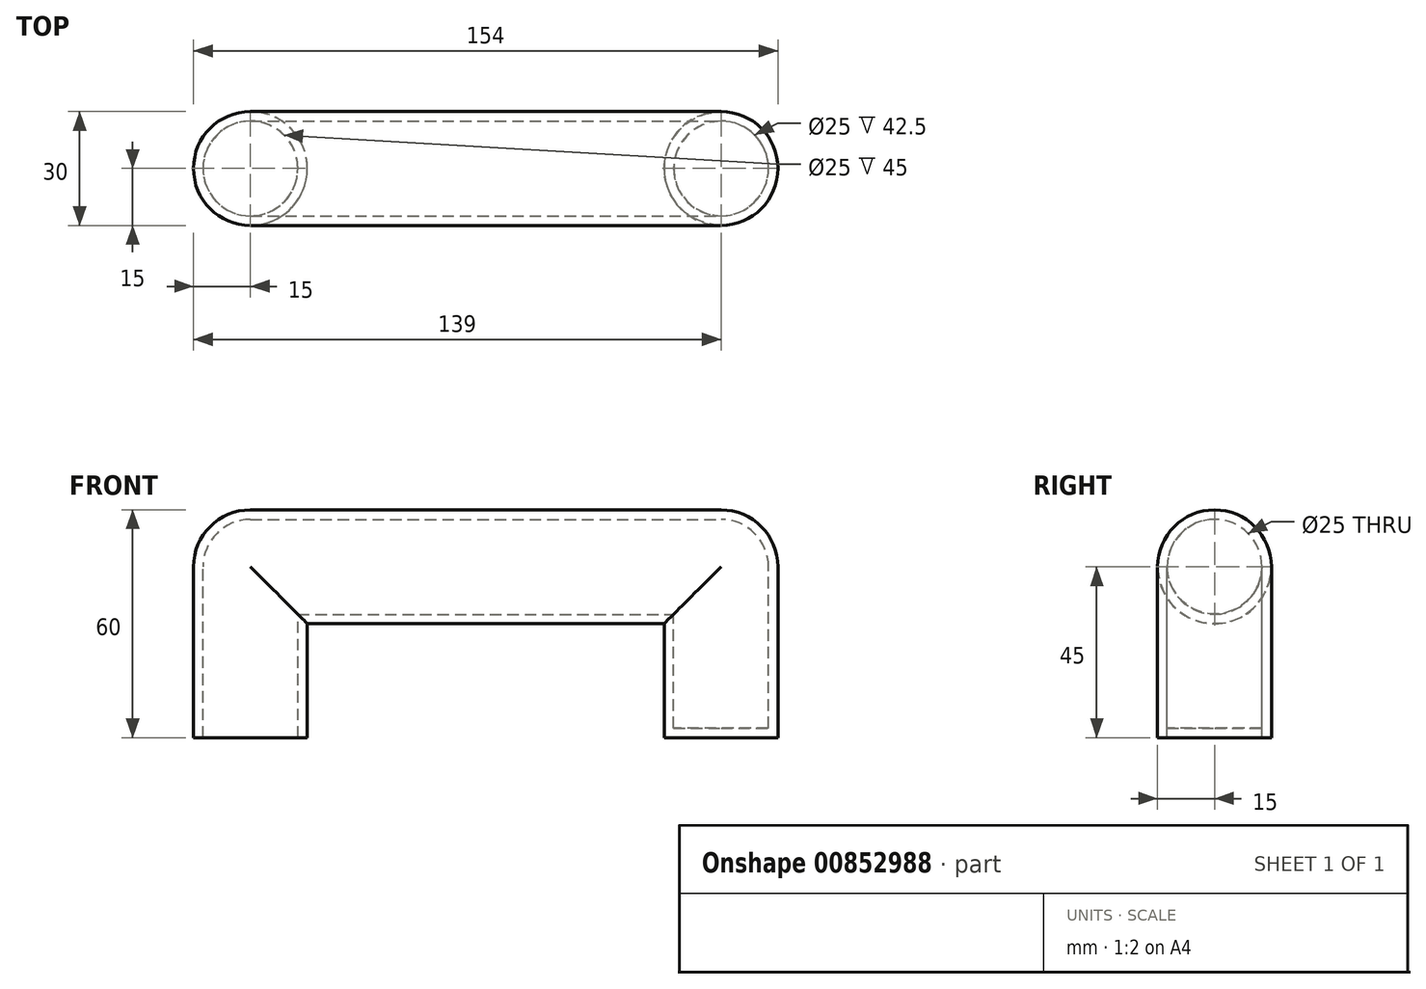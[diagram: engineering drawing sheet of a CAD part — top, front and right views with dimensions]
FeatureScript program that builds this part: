
annotation { "Feature Type Name" : "Feature", "Feature Type Description" : "" }
export const myFeature = defineFeature(function(context is Context, id is Id, definition is map)
    precondition{}
    {
        {
            var Q0;
            Q0=qCreatedBy(makeId("Front.planeOp"),FACE);
            var sketch = newSketch(context, id + "F0", { "sketchPlane" : qUnion([Q0])});
            skLineSegment(sketch, "E0.bottom", {"start": v(0, 0) * mm, "end": v(30, 0) * mm});
            skLineSegment(sketch, "E0.top", {"start": v(0, 60) * mm, "end": v(154, 60) * mm});
            skLineSegment(sketch, "E0.left", {"start": v(0, 0) * mm, "end": v(0, 60) * mm});
            skLineSegment(sketch, "E0.right", {"start": v(154, 0) * mm, "end": v(154, 60) * mm});
            skLineSegment(sketch, "E1.left", {"start": v(0, -22.26) * mm, "end": v(0, 0) * mm});
            skLineSegment(sketch, "E1.right", {"start": v(30, 0) * mm, "end": v(30, 30) * mm});
            skLineSegment(sketch, "E2.bottom", {"start": v(154, 0) * mm, "end": v(124, 0) * mm});
            skLineSegment(sketch, "E2.left", {"start": v(154, -22.26) * mm, "end": v(154, 0) * mm});
            skLineSegment(sketch, "E2.right", {"start": v(124, 0) * mm, "end": v(124, 30) * mm});
            skLineSegment(sketch, "E3", {"start": v(30, 30) * mm, "end": v(124, 30) * mm});
            skLineSegment(sketch, "E4.trimOffspring", {"start": v(124, 0) * mm, "end": v(154, 0) * mm});
            skSolve(sketch);
        }
        {
            var Q0;
            Q0=makeQuery(id+"F0.imprint","IMPRINT",FACE,{"disambiguationData":[TD([[makeQuery(id+"F0.imprint","IMPRINT",EDGE,{"derivedFrom":sQuery(id+"F0.wireOp",EDGE,"E0.top")}),-1.0]])]});
            extrude(context, id + "F1", {"entities" : qUnion([Q0]), "depth" : 30 * mm, "offsetDistance" : 25 * mm});
        }
        {
            var Q0;
            Q0=makeQuery(id+"F1.opExtrude","SWEPT_FACE",FACE,{"disambiguationData":[OSD([sQuery(id+"F0.wireOp",EDGE,"E0.top")])]});
            var Q1;
            Q1=makeQuery(id+"F1.opExtrude","CAP_EDGE",EDGE,{"disambiguationData":[OSD([sQuery(id+"F0.wireOp",EDGE,"E0.right"),sQuery(id+"F0.wireOp",EDGE,"E2.left")])],"isStart":false});
            var Q2;
            Q2=makeQuery(id+"F1.opExtrude","CAP_EDGE",EDGE,{"disambiguationData":[OSD([sQuery(id+"F0.wireOp",EDGE,"E2.right")])],"isStart":false});
            var Q3;
            Q3=makeQuery(id+"F1.opExtrude","CAP_EDGE",EDGE,{"disambiguationData":[OSD([sQuery(id+"F0.wireOp",EDGE,"E3")])],"isStart":false});
            var Q4;
            Q4=makeQuery(id+"F1.opExtrude","CAP_EDGE",EDGE,{"disambiguationData":[OSD([sQuery(id+"F0.wireOp",EDGE,"E1.right")])],"isStart":false});
            var Q5;
            Q5=makeQuery(id+"F1.opExtrude","CAP_EDGE",EDGE,{"disambiguationData":[OSD([sQuery(id+"F0.wireOp",EDGE,"E0.right"),sQuery(id+"F0.wireOp",EDGE,"E2.left")])],"isStart":true});
            var Q6;
            Q6=makeQuery(id+"F1.opExtrude","CAP_EDGE",EDGE,{"disambiguationData":[OSD([sQuery(id+"F0.wireOp",EDGE,"E2.right")])],"isStart":true});
            var Q7;
            Q7=makeQuery(id+"F1.opExtrude","CAP_EDGE",EDGE,{"disambiguationData":[OSD([sQuery(id+"F0.wireOp",EDGE,"E1.right")])],"isStart":true});
            var Q8;
            Q8=makeQuery(id+"F1.opExtrude","CAP_EDGE",EDGE,{"disambiguationData":[OSD([sQuery(id+"F0.wireOp",EDGE,"E3")])],"isStart":true});
            var Q9;
            Q9=makeQuery(id+"F1.opExtrude","CAP_EDGE",EDGE,{"disambiguationData":[OSD([sQuery(id+"F0.wireOp",EDGE,"E0.left"),sQuery(id+"F0.wireOp",EDGE,"E1.left")])],"isStart":true});
            var Q10;
            Q10=makeQuery(id+"F1.opExtrude","CAP_EDGE",EDGE,{"disambiguationData":[OSD([sQuery(id+"F0.wireOp",EDGE,"E0.left"),sQuery(id+"F0.wireOp",EDGE,"E1.left")])],"isStart":false});
            fillet(context, id + "F2", {"entities" : qUnion([Q0, Q1, Q2, Q3, Q4, Q5, Q6, Q7, Q8, Q9, Q10]), "radius" : 15 * mm, "allowEdgeOverflow" : false});
        }
        {
            var Q0;
            Q0=makeQuery(id+"F1.opExtrude","SWEPT_FACE",FACE,{"disambiguationData":[OSD([sQuery(id+"F0.wireOp",EDGE,"E0.bottom")])]});
            var Q1;
            Q1=makeQuery(id+"F1.opExtrude","SWEPT_FACE",FACE,{"disambiguationData":[OSD([sQuery(id+"F0.wireOp",EDGE,"E4.trimOffspring")])]});
            shell(context, id + "F3", {"entities" : qUnion([Q0, Q1]), "thickness" : 2.5 * mm});
        }
    });
